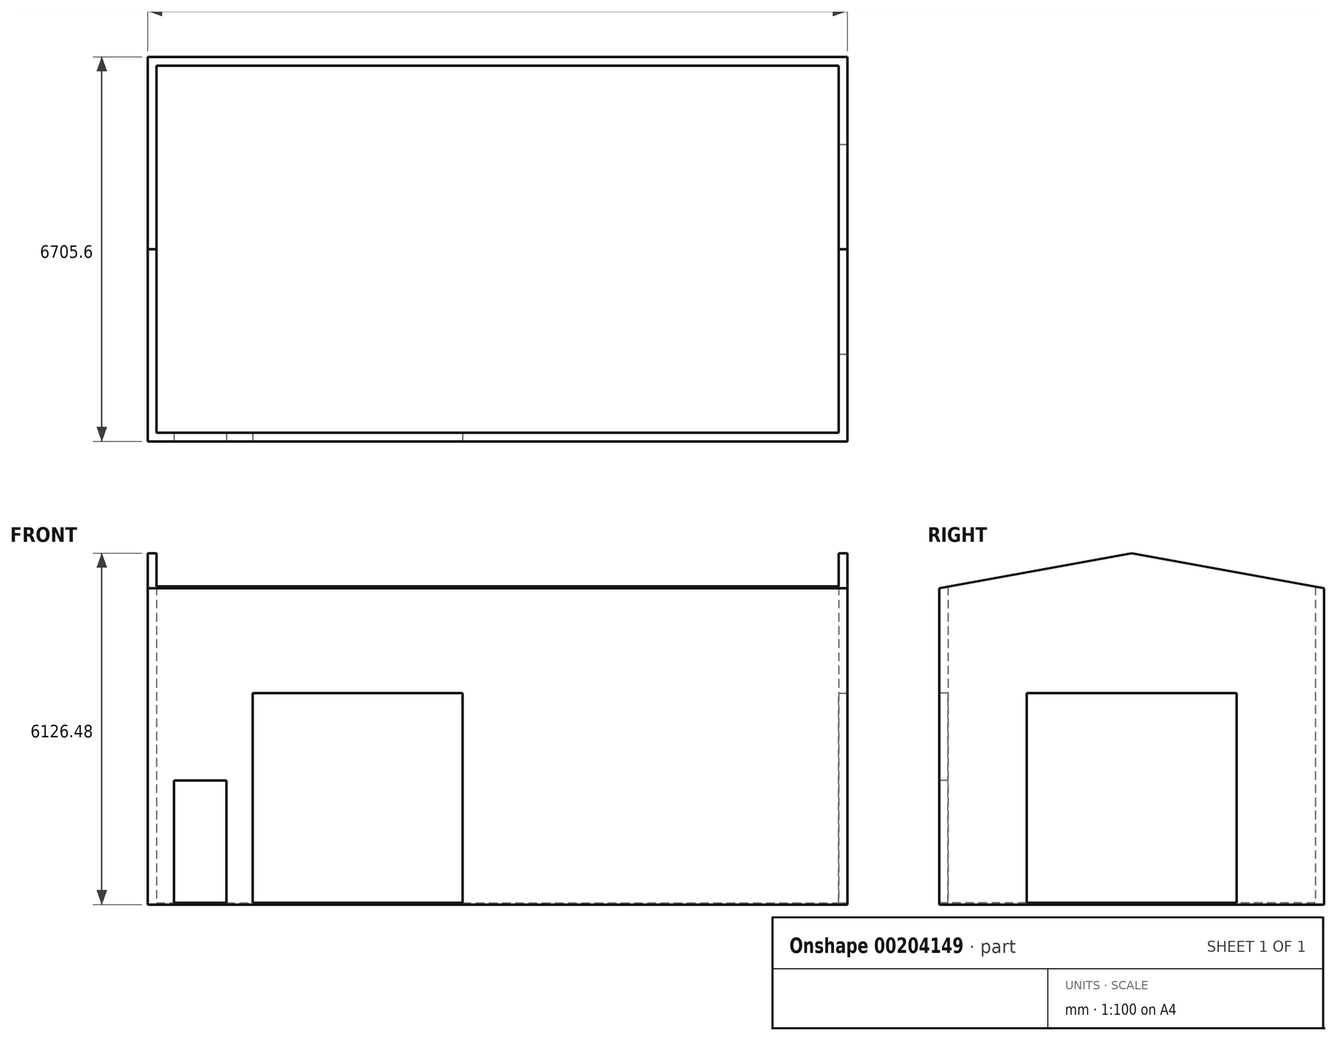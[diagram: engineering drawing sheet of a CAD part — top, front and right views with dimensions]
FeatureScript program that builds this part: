
annotation { "Feature Type Name" : "Feature", "Feature Type Description" : "" }
export const myFeature = defineFeature(function(context is Context, id is Id, definition is map)
    precondition{}
    {
        {
            var Q0;
            Q0=qCreatedBy(makeId("Top.planeOp"),FACE);
            var sketch = newSketch(context, id + "F0", { "sketchPlane" : qUnion([Q0])});
            skLineSegment(sketch, "E0.bottom", {"start": v(0, 0) * mm, "end": v(12192, 0) * mm});
            skLineSegment(sketch, "E0.top", {"start": v(0, 6705.6) * mm, "end": v(12192, 6705.6) * mm});
            skLineSegment(sketch, "E0.left", {"start": v(0, 0) * mm, "end": v(0, 6705.6) * mm});
            skLineSegment(sketch, "E0.right", {"start": v(12192, 0) * mm, "end": v(12192, 6705.6) * mm});
            skSolve(sketch);
        }
        {
            var Q0;
            Q0 = qSketchRegion(id + "F0", true);
            extrude(context, id + "F1", {"entities" : qUnion([Q0]), "depth" : 30.48 * mm});
        }
        {
            var Q0;
            Q0=makeQuery(id+"F1.opExtrude","CAP_FACE",FACE,{"disambiguationData":[OSD([sQuery(id+"F0.wireOp",EDGE,"E0.bottom"),sQuery(id+"F0.wireOp",EDGE,"E0.top"),sQuery(id+"F0.wireOp",EDGE,"E0.left"),sQuery(id+"F0.wireOp",EDGE,"E0.right")])],"isStart":false});
            var sketch = newSketch(context, id + "F2", { "sketchPlane" : qUnion([Q0])});
            skLineSegment(sketch, "E1.bottom", {"start": v(0, 6705.6) * mm, "end": v(152.4, 6705.6) * mm});
            skLineSegment(sketch, "E1.top", {"start": v(0, 0) * mm, "end": v(152.4, 0) * mm});
            skLineSegment(sketch, "E1.left", {"start": v(0, 6705.6) * mm, "end": v(0, 0) * mm});
            skLineSegment(sketch, "E1.right", {"start": v(152.4, 6705.6) * mm, "end": v(152.4, 0) * mm});
            skLineSegment(sketch, "E2.bottom", {"start": v(152.4, 6705.6) * mm, "end": v(12192, 6705.6) * mm});
            skLineSegment(sketch, "E2.top", {"start": v(152.4, 6553.2) * mm, "end": v(12192, 6553.2) * mm});
            skLineSegment(sketch, "E2.left", {"start": v(152.4, 6705.6) * mm, "end": v(152.4, 6553.2) * mm});
            skLineSegment(sketch, "E2.right", {"start": v(12192, 6705.6) * mm, "end": v(12192, 6553.2) * mm});
            skLineSegment(sketch, "E3.bottom", {"start": v(12192, 6553.2) * mm, "end": v(12039.6, 6553.2) * mm});
            skLineSegment(sketch, "E3.top", {"start": v(12192, 0) * mm, "end": v(12039.6, 0) * mm});
            skLineSegment(sketch, "E3.left", {"start": v(12192, 6553.2) * mm, "end": v(12192, 0) * mm});
            skLineSegment(sketch, "E3.right", {"start": v(12039.6, 6553.2) * mm, "end": v(12039.6, 0) * mm});
            skLineSegment(sketch, "E4.bottom", {"start": v(152.4, 0) * mm, "end": v(12039.6, 0) * mm});
            skLineSegment(sketch, "E4.top", {"start": v(152.4, 152.4) * mm, "end": v(12039.6, 152.4) * mm});
            skLineSegment(sketch, "E4.left", {"start": v(152.4, 0) * mm, "end": v(152.4, 152.4) * mm});
            skLineSegment(sketch, "E4.right", {"start": v(12039.6, 0) * mm, "end": v(12039.6, 152.4) * mm});
            skSolve(sketch);
        }
        {
            var Q0;
            Q0 = qSketchRegion(id + "F2", true);
            extrude(context, id + "F3", {"entities" : qUnion([Q0]), "operationType" : NewBodyOperationType.ADD, "depth" : 6096 * mm});
        }
        {
            var Q0;
            Q0=makeQuery(id+"F3.boolean.opBoolean","MERGE",FACE,{"derivedFrom":[makeQuery(id+"F1.opExtrude","SWEPT_FACE",FACE,{"disambiguationData":[OSD([sQuery(id+"F0.wireOp",EDGE,"E0.right")])]}),makeQuery(id+"F3.opExtrude","SWEPT_FACE",FACE,{"disambiguationData":[OSD([sQuery(id+"F2.wireOp",EDGE,"E2.right"),sQuery(id+"F2.wireOp",EDGE,"E3.left")])]})]});
            var sketch = newSketch(context, id + "F4", { "sketchPlane" : qUnion([Q0])});
            skLineSegment(sketch, "E5", {"start": v(0, 6126.48) * mm, "end": v(3352.8, 6126.48) * mm});
            skLineSegment(sketch, "E6", {"start": v(3352.8, 6126.48) * mm, "end": v(0, 5516.88) * mm});
            skLineSegment(sketch, "E7", {"start": v(0, 5516.88) * mm, "end": v(0, 6126.48) * mm});
            skLineSegment(sketch, "E8", {"start": v(3352.8, 6126.48) * mm, "end": v(6705.6, 5516.88) * mm});
            skLineSegment(sketch, "E9", {"start": v(6705.6, 5516.88) * mm, "end": v(6705.6, 6126.48) * mm});
            skLineSegment(sketch, "E10", {"start": v(6705.6, 6126.48) * mm, "end": v(3352.8, 6126.48) * mm});
            skSolve(sketch);
        }
        {
            var Q0;
            Q0 = qSketchRegion(id + "F4", true);
            extrude(context, id + "F5", {"entities" : qUnion([Q0]), "operationType" : NewBodyOperationType.REMOVE, "endBound" : BoundingType.THROUGH_ALL, "oppositeDirection" : true, "depth" : 30.48 * mm});
        }
        {
            var Q0;
            Q0=makeQuery(id+"F3.boolean.opBoolean","MERGE",FACE,{"derivedFrom":[makeQuery(id+"F1.opExtrude","SWEPT_FACE",FACE,{"disambiguationData":[OSD([sQuery(id+"F0.wireOp",EDGE,"E0.right")])]}),makeQuery(id+"F3.opExtrude","SWEPT_FACE",FACE,{"disambiguationData":[OSD([sQuery(id+"F2.wireOp",EDGE,"E2.right"),sQuery(id+"F2.wireOp",EDGE,"E3.left")])]})]});
            var sketch = newSketch(context, id + "F6", { "sketchPlane" : qUnion([Q0])});
            skLineSegment(sketch, "E11.bottom", {"start": v(1524, 30.48) * mm, "end": v(5181.6, 30.48) * mm});
            skLineSegment(sketch, "E11.top", {"start": v(1524, 3688.08) * mm, "end": v(5181.6, 3688.08) * mm});
            skLineSegment(sketch, "E11.left", {"start": v(1524, 30.48) * mm, "end": v(1524, 3688.08) * mm});
            skLineSegment(sketch, "E11.right", {"start": v(5181.6, 30.48) * mm, "end": v(5181.6, 3688.08) * mm});
            skSolve(sketch);
        }
        {
            var Q0;
            Q0 = qSketchRegion(id + "F6", true);
            extrude(context, id + "F7", {"entities" : qUnion([Q0]), "operationType" : NewBodyOperationType.REMOVE, "oppositeDirection" : true, "depth" : 152.4 * mm});
        }
        {
            var Q0;
            Q0=makeQuery(id+"F3.boolean.opBoolean","MERGE",FACE,{"derivedFrom":[makeQuery(id+"F1.opExtrude","SWEPT_FACE",FACE,{"disambiguationData":[OSD([sQuery(id+"F0.wireOp",EDGE,"E0.bottom")])]}),makeQuery(id+"F3.opExtrude","SWEPT_FACE",FACE,{"disambiguationData":[OSD([sQuery(id+"F2.wireOp",EDGE,"E1.top"),sQuery(id+"F2.wireOp",EDGE,"E3.top"),sQuery(id+"F2.wireOp",EDGE,"E4.bottom")])]})]});
            var sketch = newSketch(context, id + "F8", { "sketchPlane" : qUnion([Q0])});
            skLineSegment(sketch, "E12.bottom", {"start": v(1828.8, 30.48) * mm, "end": v(5486.4, 30.48) * mm});
            skLineSegment(sketch, "E12.top", {"start": v(1828.8, 3688.08) * mm, "end": v(5486.4, 3688.08) * mm});
            skLineSegment(sketch, "E12.left", {"start": v(1828.8, 30.48) * mm, "end": v(1828.8, 3688.08) * mm});
            skLineSegment(sketch, "E12.right", {"start": v(5486.4, 30.48) * mm, "end": v(5486.4, 3688.08) * mm});
            skSolve(sketch);
        }
        {
            var Q0;
            Q0 = qSketchRegion(id + "F8", true);
            extrude(context, id + "F9", {"entities" : qUnion([Q0]), "operationType" : NewBodyOperationType.REMOVE, "oppositeDirection" : true, "depth" : 152.4 * mm});
        }
        {
            var Q0;
            Q0=makeQuery(id+"F3.boolean.opBoolean","MERGE",FACE,{"derivedFrom":[makeQuery(id+"F1.opExtrude","SWEPT_FACE",FACE,{"disambiguationData":[OSD([sQuery(id+"F0.wireOp",EDGE,"E0.bottom")])]}),makeQuery(id+"F3.opExtrude","SWEPT_FACE",FACE,{"disambiguationData":[OSD([sQuery(id+"F2.wireOp",EDGE,"E1.top"),sQuery(id+"F2.wireOp",EDGE,"E3.top"),sQuery(id+"F2.wireOp",EDGE,"E4.bottom")])]})]});
            var sketch = newSketch(context, id + "F10", { "sketchPlane" : qUnion([Q0])});
            skLineSegment(sketch, "E13.bottom", {"start": v(457.2, 30.48) * mm, "end": v(1371.6, 30.48) * mm});
            skLineSegment(sketch, "E13.top", {"start": v(457.2, 2164.08) * mm, "end": v(1371.6, 2164.08) * mm});
            skLineSegment(sketch, "E13.left", {"start": v(457.2, 30.48) * mm, "end": v(457.2, 2164.08) * mm});
            skLineSegment(sketch, "E13.right", {"start": v(1371.6, 30.48) * mm, "end": v(1371.6, 2164.08) * mm});
            skSolve(sketch);
        }
        {
            var Q0;
            Q0 = qSketchRegion(id + "F10", true);
            extrude(context, id + "F11", {"entities" : qUnion([Q0]), "operationType" : NewBodyOperationType.REMOVE, "oppositeDirection" : true, "depth" : 152.4 * mm});
        }
    });
